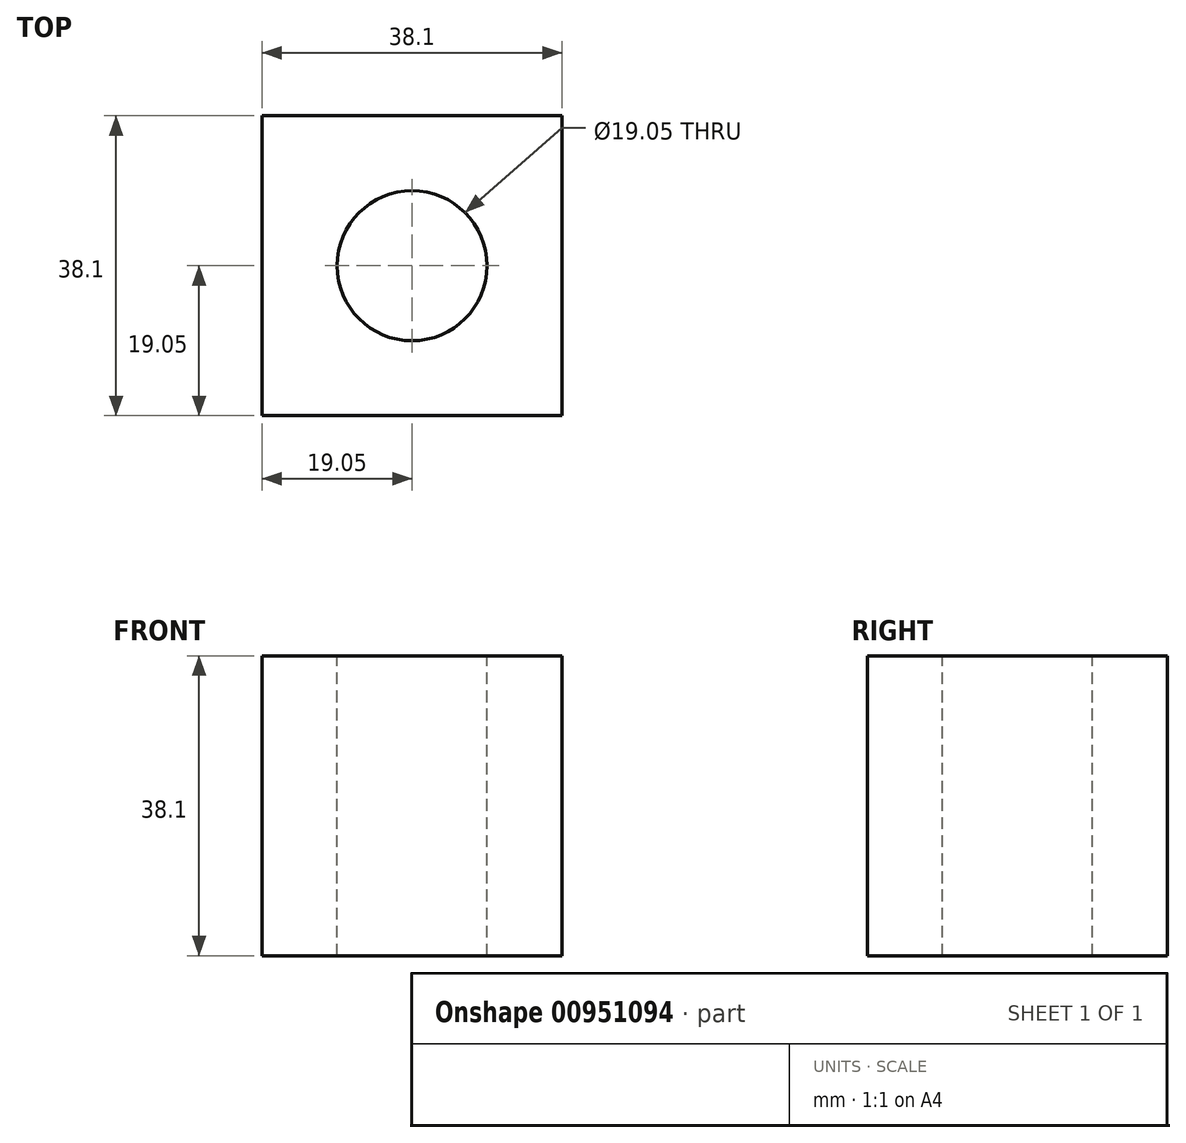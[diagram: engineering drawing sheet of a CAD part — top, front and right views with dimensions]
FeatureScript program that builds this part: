
annotation { "Feature Type Name" : "Feature", "Feature Type Description" : "" }
export const myFeature = defineFeature(function(context is Context, id is Id, definition is map)
    precondition{}
    {
        {
            var Q0;
            Q0=qCreatedBy(makeId("Top.planeOp"),FACE);
            var sketch = newSketch(context, id + "F0", { "sketchPlane" : qUnion([Q0])});
            skLineSegment(sketch, "E0.bottom", {"start": v(19.05, 19.05) * mm, "end": v(-19.05, 19.05) * mm});
            skLineSegment(sketch, "E0.top", {"start": v(19.05, -19.05) * mm, "end": v(-19.05, -19.05) * mm});
            skLineSegment(sketch, "E0.left", {"start": v(19.05, 19.05) * mm, "end": v(19.05, -19.05) * mm});
            skLineSegment(sketch, "E0.right", {"start": v(-19.05, 19.05) * mm, "end": v(-19.05, -19.05) * mm});
            skPoint(sketch, "E0.middle", {"position": v(0, 0) * mm});
            skSolve(sketch);
        }
        {
            var Q0;
            Q0=makeQuery(id+"F0.imprint","IMPRINT",FACE,{"disambiguationData":[TD([[makeQuery(id+"F0.imprint","IMPRINT",EDGE,{"derivedFrom":sQuery(id+"F0.wireOp",EDGE,"E0.bottom")}),1.0]])]});
            extrude(context, id + "F1", {"entities" : qUnion([Q0]), "endBound" : BoundingType.SYMMETRIC, "depth" : 38.1 * mm, "offsetDistance" : 25.4 * mm});
        }
        {
            var Q0;
            Q0=makeQuery(id+"F1.opExtrude","CAP_FACE",FACE,{"disambiguationData":[OSD([sQuery(id+"F0.wireOp",EDGE,"E0.bottom"),sQuery(id+"F0.wireOp",EDGE,"E0.top"),sQuery(id+"F0.wireOp",EDGE,"E0.left"),sQuery(id+"F0.wireOp",EDGE,"E0.right")])],"isStart":false});
            var sketch = newSketch(context, id + "F2", { "sketchPlane" : qUnion([Q0])});
            skCircle(sketch, "E1", {"center": v(0, 0) * mm, "radius": 9.53 * mm});
            skSolve(sketch);
        }
        {
            var Q0;
            Q0=makeQuery(id+"F2.imprint","IMPRINT",FACE,{"disambiguationData":[TD([[makeQuery(id+"F2.imprint","IMPRINT",EDGE,{"derivedFrom":sQuery(id+"F2.wireOp",EDGE,"E1")}),1.0]])]});
            extrude(context, id + "F3", {"entities" : qUnion([Q0]), "operationType" : NewBodyOperationType.REMOVE, "endBound" : BoundingType.THROUGH_ALL, "oppositeDirection" : true, "depth" : 25.4 * mm, "offsetDistance" : 25.4 * mm});
        }
        {
            var Q0;
            Q0=qCreatedBy(makeId("Top.planeOp"),FACE);
            var sketch = newSketch(context, id + "F4", { "sketchPlane" : qUnion([Q0])});
            skLineSegment(sketch, "E2", {"start": v(-43.36, 0) * mm, "end": v(48.13, 0) * mm});
            skLineSegment(sketch, "E3", {"start": v(0, -78.32) * mm, "end": v(0, 61.87) * mm});
            skSolve(sketch);
        }
    });
